# Revit family: QF_True_TWT-60-32-HC
name_source: partatom
category: Specialty Equipment
revit_build: Autodesk Revit 2018 (Build: 20190510_1515(x64)
units: mm (PartAtom-declared; Revit-internal decimal feet)

## family parameters
Always vertical = Yes
Cut with Voids When Loaded = No
OmniClass Number = 23.40.40.11.11.11
OmniClass Title = Refrigerators
Part Type = Normal
Room Calculation Point = No
Round Connector Dimension = Use Diameter
Shared = No
Work Plane-Based = No

## types (1)
- QF_True_TWT-60-32-HC
    Apparent Power = 196 VA
    Assembly Code = E1090320
    BTUH = 897.0 Btu/h
    CSI MasterFormat = 11 41 13
    Conn Conduit = No
    Conn Plug = NEMA 5-15P
    Cycle = 60 Hz
    Depth = 2' - 8 3/8"
    Description = Refrigerator, Worktop
    Elec Conn Connection Height = 0' - 10"
    Elec Conn RI Height = 0' - 0"
    Electric Connection Type = Plug
    FL Amps = 2 A
    Foodservice Equipment Identifier = Yes
    HP = 1/10
    Identify Quantity as Lot = Yes
    Manufacturer = True Manufacturing
    Masterspec = Divison 11
    Max Overcurrent Protection = 7 A
    Min Ckt Ampacity = 2 A
    Model = TWT-60-32-HC
    Number of Poles = 1
    Phase = 1
    Refrigerant Type = R290
    Refrigerant Volume = 0.000163 kip
    Specification by Manufacturer = Deep Work Top Refrigerator, two-section, stainless steel top with rear splash, (2) stainless steel doors, (4) PVC coated adjustable wire shelves, stainless steel front & sides, aluminum interior with stainless steel floor, 5" castors, side mount front breather, R290 Hydrocarbon refrigerant, 1/10 HP, 115v/60/1-ph, 1.7 amps, NEMA 5-15P, cULus, UL EPH Classified, Made in USA contact factory for price
    URL = https://www.truemfg.com
    URL Cutsheet = https://dc2kentprodcontent.blob.core.windows.net
    Volts = 115 V
    Watts = 196 W
    Weight in Pounds = 415
    Width = 5' - 0 1/4"

## geometry (parser evidence)
native form markers: Sweep x26
no freeform markers — native parametric forms only
